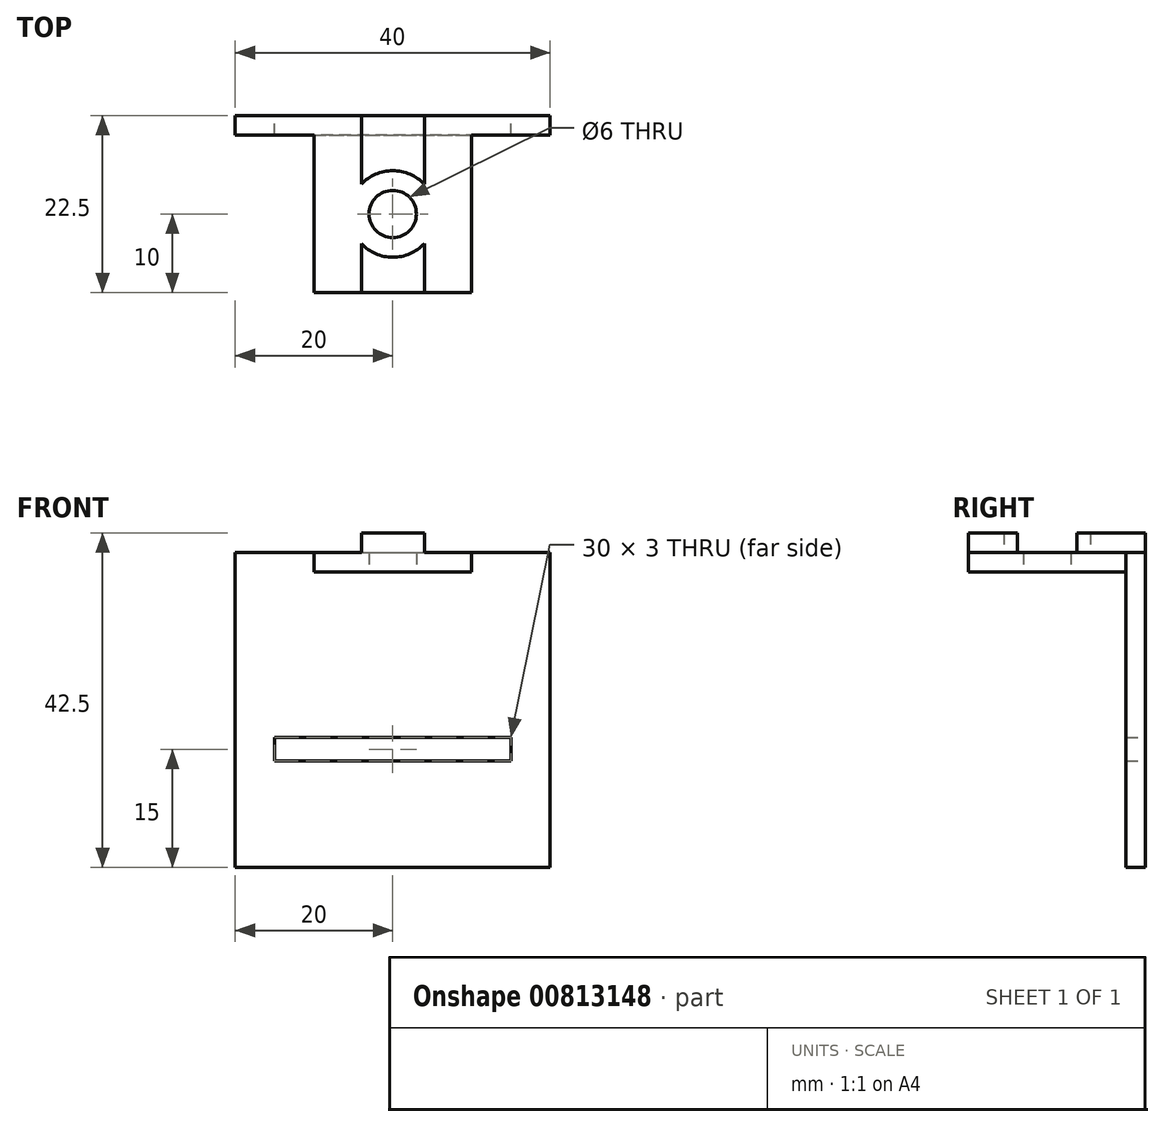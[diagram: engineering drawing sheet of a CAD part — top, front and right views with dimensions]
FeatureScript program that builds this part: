
annotation { "Feature Type Name" : "Feature", "Feature Type Description" : "" }
export const myFeature = defineFeature(function(context is Context, id is Id, definition is map)
    precondition{}
    {
        {
            var Q0;
            Q0=qCreatedBy(makeId("Front.planeOp"),FACE);
            var sketch = newSketch(context, id + "F0", { "sketchPlane" : qUnion([Q0])});
            skLineSegment(sketch, "E0.bottom", {"start": v(20, -20) * mm, "end": v(-20, -20) * mm});
            skLineSegment(sketch, "E0.top", {"start": v(20, 20) * mm, "end": v(10, 20) * mm});
            skLineSegment(sketch, "E0.left", {"start": v(20, -20) * mm, "end": v(20, 20) * mm});
            skLineSegment(sketch, "E0.right", {"start": v(-20, -20) * mm, "end": v(-20, 20) * mm});
            skPoint(sketch, "E0.middle", {"position": v(0, 0) * mm});
            skLineSegment(sketch, "E1.bottom", {"start": v(-20, 20) * mm, "end": v(4, 20) * mm});
            skLineSegment(sketch, "E1.left", {"start": v(-20, 20) * mm, "end": v(-20, 17.5) * mm});
            skLineSegment(sketch, "E1.right", {"start": v(20, 20) * mm, "end": v(20, 17.5) * mm});
            skLineSegment(sketch, "E2", {"start": v(-4, 20) * mm, "end": v(-4, 22.5) * mm});
            skLineSegment(sketch, "E3", {"start": v(-4, 22.5) * mm, "end": v(4, 22.5) * mm});
            skLineSegment(sketch, "E4", {"start": v(4, 22.5) * mm, "end": v(4, 20) * mm});
            skLineSegment(sketch, "E5.bottom", {"start": v(-15, -3.5) * mm, "end": v(15, -3.5) * mm});
            skLineSegment(sketch, "E5.top", {"start": v(-15, -6.5) * mm, "end": v(15, -6.5) * mm});
            skLineSegment(sketch, "E5.left", {"start": v(-15, -3.5) * mm, "end": v(-15, -6.5) * mm});
            skLineSegment(sketch, "E5.right", {"start": v(15, -3.5) * mm, "end": v(15, -6.5) * mm});
            skPoint(sketch, "E5.middle", {"position": v(0, -5) * mm});
            skLineSegment(sketch, "E6", {"start": v(-10, 20) * mm, "end": v(-10, 17.5) * mm});
            skLineSegment(sketch, "E7", {"start": v(-10, 17.5) * mm, "end": v(0, 17.5) * mm});
            skLineSegment(sketch, "E8.MirrorCS", {"start": v(10, 17.5) * mm, "end": v(0, 17.5) * mm});
            skLineSegment(sketch, "E9.MirrorCS", {"start": v(10, 20) * mm, "end": v(10, 17.5) * mm});
            skLineSegment(sketch, "E10.trimOffspring", {"start": v(4, 20) * mm, "end": v(-20, 20) * mm});
            skLineSegment(sketch, "E11", {"start": v(4, 20) * mm, "end": v(10, 20) * mm});
            skSolve(sketch);
        }
        {
            var Q0;
            Q0=makeQuery(id+"F0.imprint","IMPRINT",FACE,{"disambiguationData":[TD([[makeQuery(id+"F0.imprint","IMPRINT",EDGE,{"derivedFrom":sQuery(id+"F0.wireOp",EDGE,"E0.bottom")}),-1.0]])]});
            extrude(context, id + "F1", {"entities" : qUnion([Q0]), "depth" : 2.5 * mm, "offsetDistance" : 25 * mm});
        }
        {
            var Q0;
            {var subQ0=sQuery(id+"F0.wireOp",EDGE,"E6");Q0=makeQuery(id+"F0.imprint","IMPRINT",FACE,{"disambiguationData":[TD([[makeQuery(id+"F0.imprint","IMPRINT",EDGE,{"derivedFrom":subQ0}),1.0]])]});}
            extrude(context, id + "F2", {"entities" : qUnion([Q0]), "operationType" : NewBodyOperationType.ADD, "depth" : 22.5 * mm, "offsetDistance" : 25 * mm});
        }
        {
            var Q0;
            {var subQ0=sQuery(id+"F0.wireOp",EDGE,"E2");Q0=makeQuery(id+"F0.imprint","IMPRINT",FACE,{"disambiguationData":[TD([[makeQuery(id+"F0.imprint","IMPRINT",EDGE,{"derivedFrom":subQ0}),-1.0]])]});}
            extrude(context, id + "F3", {"entities" : qUnion([Q0]), "operationType" : NewBodyOperationType.ADD, "depth" : 22.5 * mm, "offsetDistance" : 25 * mm});
        }
        {
            var Q0;
            Q0=makeQuery(id+"F2.opExtrude","SWEPT_FACE",FACE,{"disambiguationData":[OSD([sQuery(id+"F0.wireOp",EDGE,"E7"),sQuery(id+"F0.wireOp",EDGE,"E8.MirrorCS")])]});
            var sketch = newSketch(context, id + "F4", { "sketchPlane" : qUnion([Q0])});
            skCircle(sketch, "E12", {"center": v(0, 12.5) * mm, "radius": 3 * mm});
            skCircle(sketch, "E13", {"center": v(0, 12.5) * mm, "radius": 5.5 * mm});
            skSolve(sketch);
        }
        {
            var Q0;
            Q0=makeQuery(id+"F4.imprint","IMPRINT",FACE,{"disambiguationData":[TD([[makeQuery(id+"F4.imprint","IMPRINT",EDGE,{"derivedFrom":sQuery(id+"F4.wireOp",EDGE,"E12")}),1.0]])]});
            extrude(context, id + "F5", {"entities" : qUnion([Q0]), "operationType" : NewBodyOperationType.REMOVE, "endBound" : BoundingType.THROUGH_ALL, "oppositeDirection" : true, "depth" : 25 * mm, "offsetDistance" : 25 * mm});
        }
        {
            var Q0;
            Q0=makeQuery(id+"F4.imprint","IMPRINT",FACE,{"disambiguationData":[TD([[makeQuery(id+"F4.imprint","IMPRINT",EDGE,{"derivedFrom":sQuery(id+"F4.wireOp",EDGE,"E12")}),-1.0]])]});
            extrude(context, id + "F6", {"entities" : qUnion([Q0]), "operationType" : NewBodyOperationType.REMOVE, "oppositeDirection" : true, "depth" : 5 * mm, "offsetDistance" : 2.5 * mm, "hasSecondDirection" : true, "secondDirectionOppositeDirection" : true, "secondDirectionDepth" : 2.5 * mm});
        }
    });
